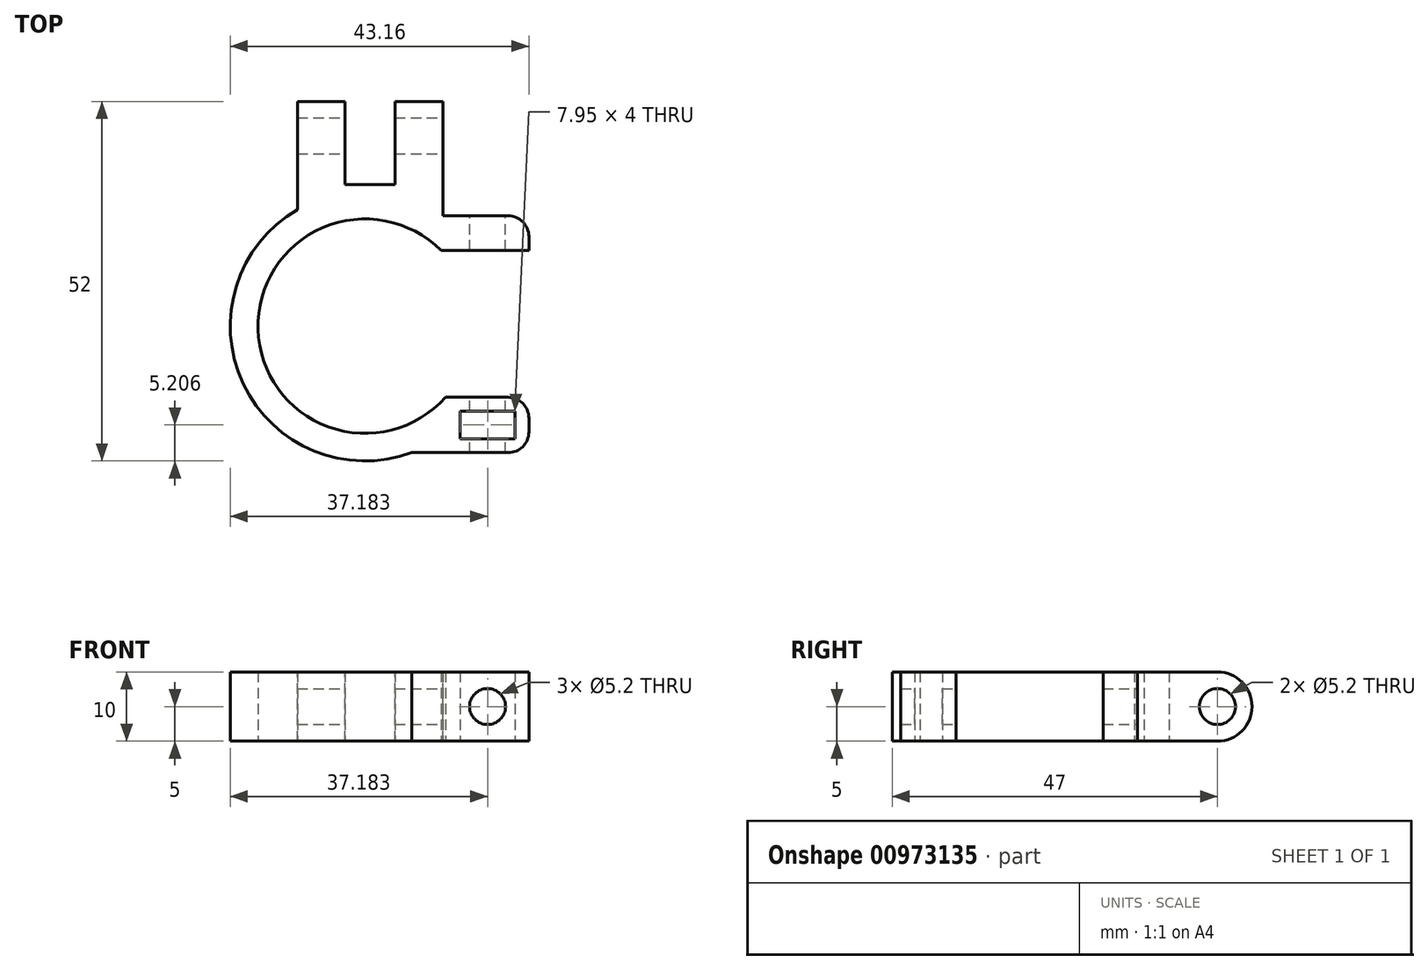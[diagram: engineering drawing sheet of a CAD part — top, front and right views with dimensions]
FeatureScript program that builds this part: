
annotation { "Feature Type Name" : "Feature", "Feature Type Description" : "" }
export const myFeature = defineFeature(function(context is Context, id is Id, definition is map)
    precondition{}
    {
        {
            var Q0;
            Q0=qCreatedBy(makeId("Top.planeOp"),FACE);
            var sketch = newSketch(context, id + "F0", { "sketchPlane" : qUnion([Q0])});
            skLineSegment(sketch, "E0", {"start": v(11.2, 15.96) * mm, "end": v(11.2, 15.96) * mm});
            skLineSegment(sketch, "E1.rect.top", {"start": v(23.66, 15.96) * mm, "end": v(11.2, 15.96) * mm});
            skLineSegment(sketch, "E1.rect.left", {"start": v(23.66, -18.3) * mm, "end": v(23.66, -10.3) * mm});
            skLineSegment(sketch, "E2.0", {"start": v(23.66, 10.96) * mm, "end": v(10.96, 10.96) * mm});
            skLineSegment(sketch, "E3.0", {"start": v(23.66, -10.3) * mm, "end": v(11.59, -10.3) * mm});
            skLineSegment(sketch, "E4.trimOffspring", {"start": v(23.66, 10.96) * mm, "end": v(23.66, 15.96) * mm});
            skCircle(sketch, "E5.converted", {"center": v(0, 0) * mm, "radius": 15.5 * mm, "construction": true});
            skArc(sketch, "E6.0", {"start": v(10.96, 10.96) * mm, "mid": v(-15.5, -0.46) * mm, "end": v(11.59, -10.3) * mm});
            skLineSegment(sketch, "E7.rect.bottom", {"start": v(-9.8, 32.5) * mm, "end": v(-2.9, 32.5) * mm});
            skLineSegment(sketch, "E7.rect.left", {"start": v(-9.8, 32.5) * mm, "end": v(-9.8, 16.86) * mm});
            skLineSegment(sketch, "E7.rect.right", {"start": v(11.2, 32.5) * mm, "end": v(11.2, 15.96) * mm});
            skPoint(sketch, "E7.rect.middle", {"position": v(0.06, 0.12) * mm});
            skLineSegment(sketch, "E8.0", {"start": v(-2.9, 20.5) * mm, "end": v(4.3, 20.5) * mm});
            skLineSegment(sketch, "E9.0", {"start": v(-2.9, 32.5) * mm, "end": v(-2.9, 19.28) * mm});
            skLineSegment(sketch, "E10.0", {"start": v(4.3, 32.5) * mm, "end": v(4.3, 19.02) * mm});
            skArc(sketch, "E11.trimOffspring", {"start": v(-9.8, 16.86) * mm, "mid": v(-17.64, -8.3) * mm, "end": v(6.75, -18.3) * mm});
            skLineSegment(sketch, "E12.trimOffspring", {"start": v(4.3, 32.5) * mm, "end": v(11.2, 32.5) * mm});
            skLineSegment(sketch, "E13.0", {"start": v(23.66, -18.3) * mm, "end": v(12.97, -18.3) * mm});
            skLineSegment(sketch, "E14", {"start": v(12.97, -18.3) * mm, "end": v(6.75, -18.3) * mm});
            skLineSegment(sketch, "E15.0", {"start": v(21.66, -16.3) * mm, "end": v(21.66, -12.3) * mm});
            skLineSegment(sketch, "E16.0", {"start": v(13.7, -16.3) * mm, "end": v(13.7, -12.3) * mm});
            skLineSegment(sketch, "E17", {"start": v(23.66, -10.3) * mm, "end": v(23.66, 10.96) * mm, "construction": true});
            skLineSegment(sketch, "E18.0", {"start": v(21.66, -16.3) * mm, "end": v(13.7, -16.3) * mm});
            skLineSegment(sketch, "E19.0", {"start": v(21.66, -12.3) * mm, "end": v(13.7, -12.3) * mm});
            skSolve(sketch);
        }
        {
            var Q0;
            Q0=qSketchRegion(id+"F0",true);
            extrude(context, id + "F1", {"entities" : qUnion([Q0]), "depth" : 10 * mm});
        }
        {
            var Q0;
            Q0=makeQuery(id+"F1.opExtrude","SWEPT_FACE",FACE,{"disambiguationData":[OSD([sQuery(id+"F0.wireOp",EDGE,"E7.rect.right")])]});
            var sketch = newSketch(context, id + "F2", { "sketchPlane" : qUnion([Q0])});
            skLineSegment(sketch, "E20.0.0", {"start": v(27.5, 0) * mm, "end": v(32.5, 0) * mm});
            skLineSegment(sketch, "E20.0.1", {"start": v(32.5, 0) * mm, "end": v(32.5, 10) * mm});
            skLineSegment(sketch, "E20.0.2", {"start": v(32.5, 10) * mm, "end": v(27.5, 10) * mm});
            skCircle(sketch, "E21", {"center": v(27.5, 5) * mm, "radius": 2.6 * mm});
            skPoint(sketch, "E21.centerSnap0", {"position": v(27.5, 10) * mm});
            skArc(sketch, "E22", {"start": v(27.5, 0) * mm, "mid": v(32.5, 5) * mm, "end": v(27.5, 10) * mm});
            skSolve(sketch);
        }
        {
            var Q0;
            Q0=qSketchRegion(id+"F2",true);
            var Q1;
            Q1=makeQuery(id+"F1.opExtrude","SWEPT_FACE",FACE,{"disambiguationData":[OSD([sQuery(id+"F0.wireOp",EDGE,"E7.rect.left")])]});
            extrude(context, id + "F3", {"entities" : qUnion([Q0]), "operationType" : NewBodyOperationType.REMOVE, "endBound" : BoundingType.UP_TO_SURFACE, "oppositeDirection" : true, "endBoundEntityFace" : qUnion([Q1]), "depth" : 25 * mm});
        }
        {
            var Q0;
            Q0=makeQuery(id+"F1.opExtrude","SWEPT_FACE",FACE,{"disambiguationData":[OSD([sQuery(id+"F0.wireOp",EDGE,"E18.0")])]});
            var sketch = newSketch(context, id + "F4", { "sketchPlane" : qUnion([Q0])});
            skLineSegment(sketch, "E23.0.0", {"start": v(-21.66, 0) * mm, "end": v(-13.7, 0) * mm, "construction": true});
            skLineSegment(sketch, "E23.0.1", {"start": v(-13.7, 0) * mm, "end": v(-13.7, 10) * mm, "construction": true});
            skLineSegment(sketch, "E23.0.2", {"start": v(-13.7, 10) * mm, "end": v(-21.66, 10) * mm, "construction": true});
            skLineSegment(sketch, "E23.0.3", {"start": v(-21.66, 10) * mm, "end": v(-21.66, 0) * mm, "construction": true});
            skCircle(sketch, "E24", {"center": v(-17.68, 5) * mm, "radius": 2.6 * mm});
            skPoint(sketch, "E24.centerSnap0", {"position": v(-13.7, 5) * mm});
            skPoint(sketch, "E24.centerSnap1", {"position": v(-17.68, 10) * mm});
            skSolve(sketch);
        }
        {
            var Q0;
            Q0=qSketchRegion(id+"F4",true);
            extrude(context, id + "F5", {"entities" : qUnion([Q0]), "operationType" : NewBodyOperationType.REMOVE, "endBound" : BoundingType.SYMMETRIC, "oppositeDirection" : true, "depth" : 100 * mm});
        }
        {
            var Q0;
            Q0=makeQuery(id+"F1.opExtrude","SWEPT_EDGE",EDGE,{"disambiguationData":[OSD([sQuery(id+"F0.wireOp",EDGE,"E1.rect.top"),sQuery(id+"F0.wireOp",EDGE,"E4.trimOffspring")])]});
            var Q1;
            Q1=makeQuery(id+"F1.opExtrude","SWEPT_EDGE",EDGE,{"disambiguationData":[OSD([sQuery(id+"F0.wireOp",EDGE,"E1.rect.left"),sQuery(id+"F0.wireOp",EDGE,"E3.0")])]});
            var Q2;
            Q2=makeQuery(id+"F1.opExtrude","SWEPT_EDGE",EDGE,{"disambiguationData":[OSD([sQuery(id+"F0.wireOp",EDGE,"E1.rect.left"),sQuery(id+"F0.wireOp",EDGE,"E13.0")])]});
            fillet(context, id + "F6", {"entities" : qUnion([Q0, Q1, Q2]), "radius" : 3 * mm, "tangentPropagation" : true, "allowEdgeOverflow" : false});
        }
    });
